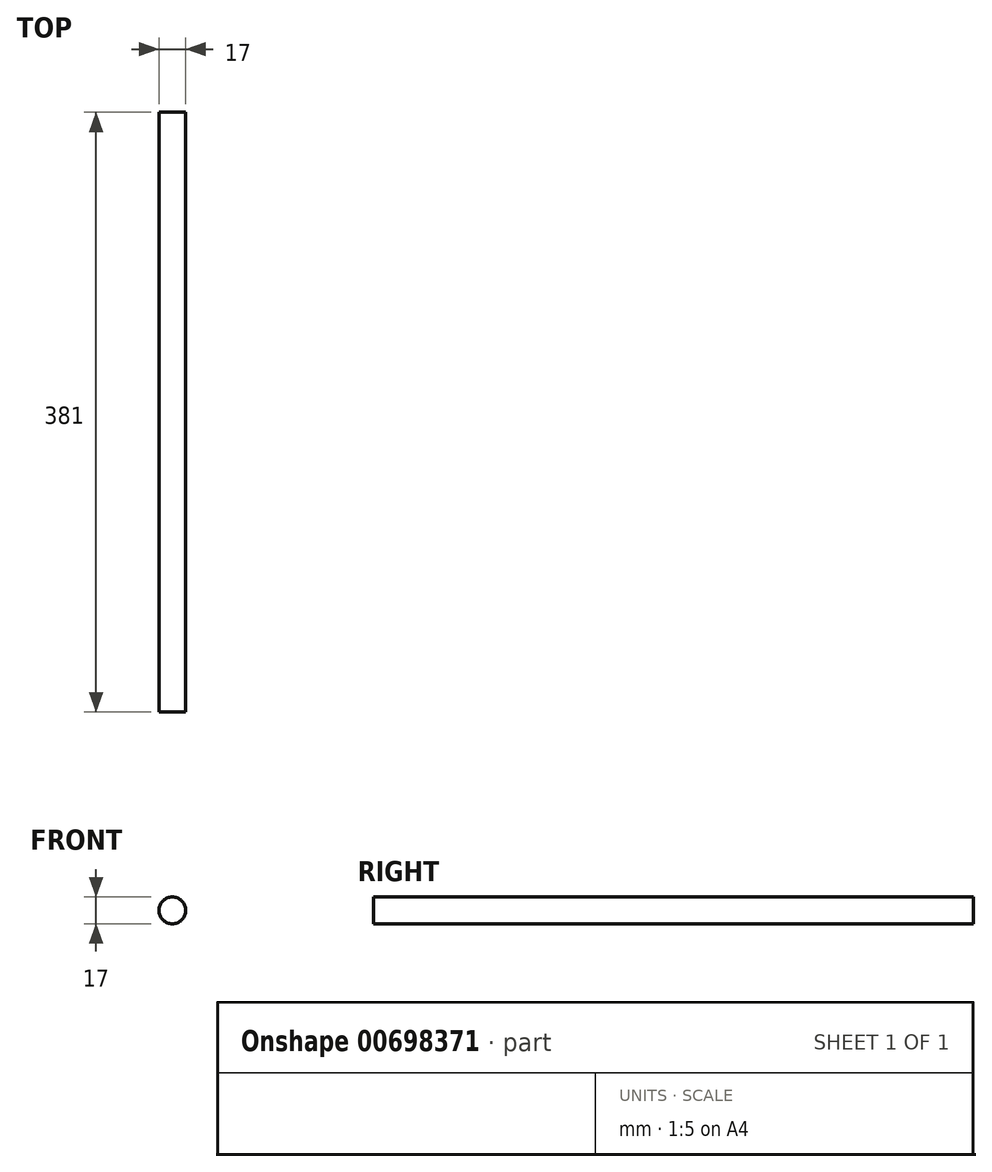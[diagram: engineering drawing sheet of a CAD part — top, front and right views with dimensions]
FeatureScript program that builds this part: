
annotation { "Feature Type Name" : "Feature", "Feature Type Description" : "" }
export const myFeature = defineFeature(function(context is Context, id is Id, definition is map)
    precondition{}
    {
        {
            var Q0;
            Q0=qCreatedBy(makeId("Front.planeOp"),FACE);
            var sketch = newSketch(context, id + "F0", { "sketchPlane" : qUnion([Q0])});
            skCircle(sketch, "E0", {"center": v(0, 0) * mm, "radius": 8.5 * mm});
            skSolve(sketch);
        }
        {
            var Q0;
            Q0=makeQuery(id+"F0.imprint","IMPRINT",FACE,{"disambiguationData":[TD([[makeQuery(id+"F0.imprint","IMPRINT",EDGE,{"derivedFrom":sQuery(id+"F0.wireOp",EDGE,"E0")}),1.0]])]});
            extrude(context, id + "F1", {"entities" : qUnion([Q0]), "depth" : 381 * mm, "offsetDistance" : 25.4 * mm});
        }
    });
